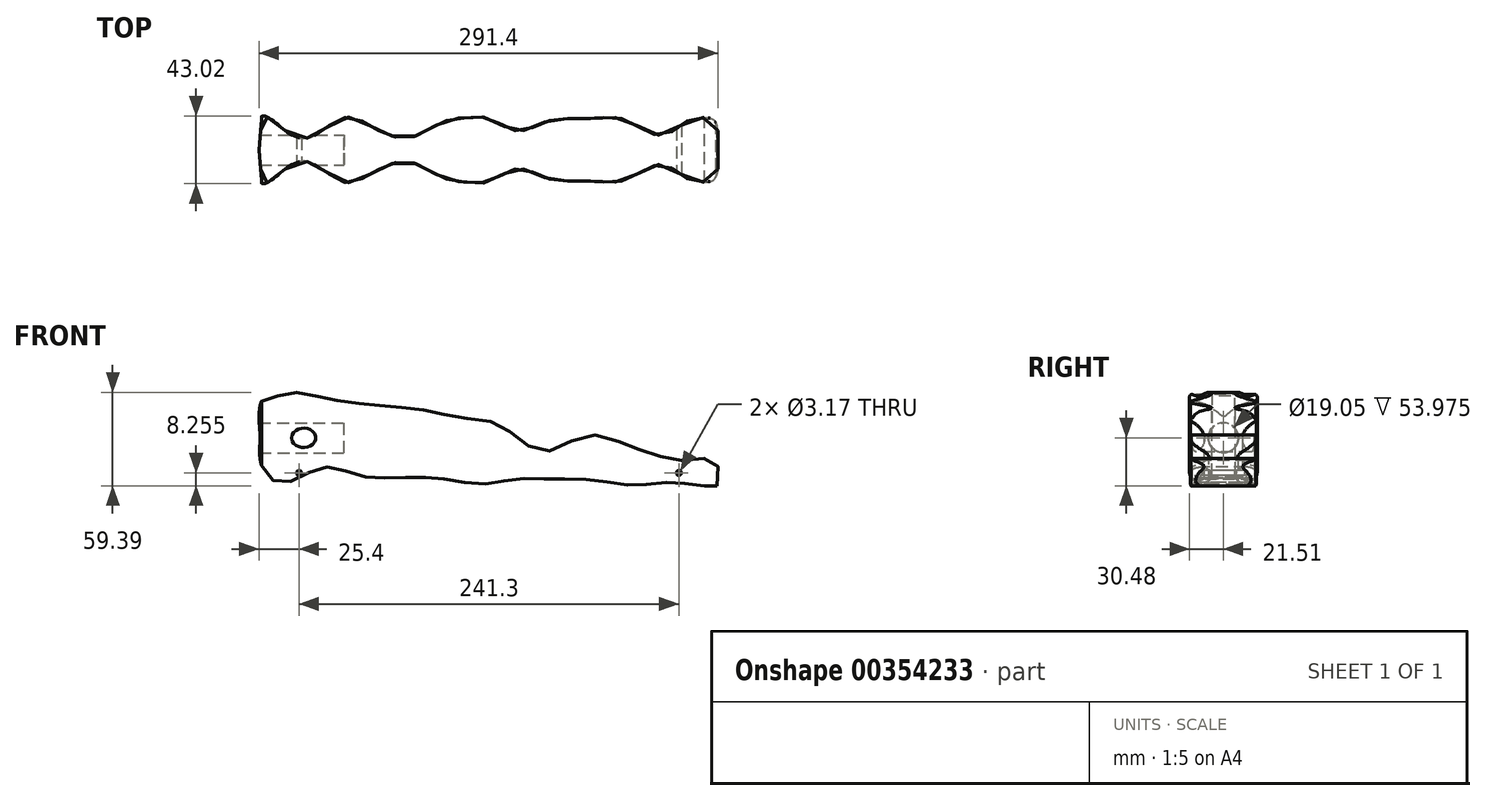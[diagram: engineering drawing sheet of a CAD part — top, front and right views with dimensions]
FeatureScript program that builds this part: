
annotation { "Feature Type Name" : "Feature", "Feature Type Description" : "" }
export const myFeature = defineFeature(function(context is Context, id is Id, definition is map)
    precondition{}
    {
        {
            var Q0;
            Q0=qCreatedBy(makeId("Front.planeOp"),FACE);
            var sketch = newSketch(context, id + "F0", { "sketchPlane" : qUnion([Q0])});
            skLineSegment(sketch, "E0.bottom", {"start": v(-146.05, 31.75) * mm, "end": v(146.05, 31.75) * mm, "construction": true});
            skLineSegment(sketch, "E0.top", {"start": v(-146.05, -31.75) * mm, "end": v(146.05, -31.75) * mm, "construction": true});
            skLineSegment(sketch, "E0.right", {"start": v(146.05, 31.75) * mm, "end": v(146.05, -31.75) * mm, "construction": true});
            skFitSpline(sketch, "E1", {"points": [v(-146.05, 0) * mm, v(-143.98, 24.56) * mm, v(-139.17, 27.47) * mm, v(-134.23, 26.49) * mm, v(-126.32, 28.75) * mm, v(-104.94, 25.5) * mm, v(-77, 21.23) * mm, v(-30.59, 15.63) * mm, v(-23.24, 12.77) * mm, v(4.3, 9.11) * mm, v(33.9, -8.77) * mm, v(59.13, 0.88) * mm, v(85.75, -3.53) * mm, v(117.37, -13.95) * mm, v(131.38, -13.42) * mm, v(144.88, -16) * mm, v(143.87, -27.24) * mm, v(144.82, -30.78) * mm, v(142.81, -31.18) * mm, v(115.14, -28.28) * mm, v(92.03, -30.12) * mm, v(63.45, -26.55) * mm, v(37.28, -26.3) * mm, v(14.94, -26.3) * mm, v(-3.83, -29.5) * mm, v(-26.85, -26.32) * mm, v(-55.1, -25.11) * mm, v(-81.78, -24.04) * mm, v(-105.32, -18.74) * mm, v(-127.18, -27.98) * mm, v(-141.83, -23.4) * mm, v(-146.05, 0) * mm]});
            skLineSegment(sketch, "E2.bottom", {"start": v(-146.05, 9.52) * mm, "end": v(-95.25, 9.52) * mm, "construction": true});
            skLineSegment(sketch, "E2.top", {"start": v(-141.83, -9.52) * mm, "end": v(-95.25, -9.52) * mm, "construction": true});
            skLineSegment(sketch, "E2.right", {"start": v(-95.25, 9.52) * mm, "end": v(-95.25, -9.52) * mm, "construction": true});
            skLineSegment(sketch, "E3", {"start": v(-146.05, 31.75) * mm, "end": v(-146.05, -31.75) * mm, "construction": true});
            skSolve(sketch);
        }
        {
            var Q0;
            Q0=qCreatedBy(makeId("Top.planeOp"),FACE);
            var sketch = newSketch(context, id + "F1", { "sketchPlane" : qUnion([Q0])});
            skLineSegment(sketch, "E4.bottom", {"start": v(-146.05, 22.22) * mm, "end": v(146.05, 22.23) * mm, "construction": true});
            skLineSegment(sketch, "E4.top", {"start": v(-146.05, -22.23) * mm, "end": v(146.05, -22.22) * mm, "construction": true});
            skLineSegment(sketch, "E4.left", {"start": v(-146.05, 22.22) * mm, "end": v(-146.05, -22.23) * mm, "construction": true});
            skLineSegment(sketch, "E4.right", {"start": v(146.05, 22.22) * mm, "end": v(146.05, -22.22) * mm, "construction": true});
            skLineSegment(sketch, "E5", {"start": v(-146.05, 0) * mm, "end": v(146.05, 0) * mm, "construction": true});
            skFitSpline(sketch, "E6", {"points": [v(-146.05, 0) * mm, v(-144.5, 19.86) * mm, v(-144.5, 21.15) * mm, v(-140.81, 20.87) * mm, v(-118.05, 7.23) * mm, v(-92.91, 20.25) * mm, v(-73.9, 14.46) * mm, v(-50.6, 7.57) * mm, v(-27.08, 18.63) * mm, v(-7.6, 20.48) * mm, v(0, 20.48) * mm, v(17.51, 12.02) * mm, v(37.61, 18.3) * mm, v(63.92, 19.8) * mm, v(86.18, 19.23) * mm, v(109.26, 9.28) * mm, v(127.86, 19.2) * mm, v(138.57, 20.35) * mm, v(143.71, 17.93) * mm, v(146.05, 0) * mm], "startDerivative": vector(0, 335.54) * mm, "endDerivative": vector(0, -277.49) * mm});
            skFitSpline(sketch, "E7.MirrorCS", {"points": [v(-146.05, 0) * mm, v(-144.5, -19.86) * mm, v(-144.5, -21.15) * mm, v(-140.81, -20.87) * mm, v(-118.05, -7.23) * mm, v(-92.91, -20.25) * mm, v(-73.9, -14.46) * mm, v(-50.6, -7.57) * mm, v(-27.08, -18.63) * mm, v(-7.6, -20.48) * mm, v(0, -20.48) * mm, v(17.51, -12.02) * mm, v(37.61, -18.3) * mm, v(63.92, -19.8) * mm, v(86.18, -19.23) * mm, v(109.26, -9.28) * mm, v(127.86, -19.2) * mm, v(138.57, -20.35) * mm, v(143.71, -17.93) * mm, v(146.05, 0) * mm], "startDerivative": vector(0, -335.54) * mm, "endDerivative": vector(0, 277.49) * mm});
            skLineSegment(sketch, "E8.MirrorCS", {"start": v(-146.05, -22.23) * mm, "end": v(146.05, -22.23) * mm});
            skSolve(sketch);
        }
        {
            var Q0;
            Q0=qCreatedBy(makeId("Right.planeOp"),FACE);
            var sketch = newSketch(context, id + "F2", { "sketchPlane" : qUnion([Q0])});
            skCircle(sketch, "E9", {"center": v(0, 0) * mm, "radius": 9.53 * mm});
            skSolve(sketch);
        }
        {
            var Q0;
            Q0=qCreatedBy(makeId("Front.planeOp"),FACE);
            var sketch = newSketch(context, id + "F3", { "sketchPlane" : qUnion([Q0])});
            skCircle(sketch, "E10", {"center": v(-120.65, -22.22) * mm, "radius": 1.59 * mm});
            skCircle(sketch, "E11", {"center": v(120.65, -22.23) * mm, "radius": 1.59 * mm});
            skSolve(sketch);
        }
        {
            var Q0;
            Q0=qSketchRegion(id+"F0",true);
            extrude(context, id + "F4", {"entities" : qUnion([Q0]), "depth" : 44.45 * mm, "symmetric" : true});
        }
        {
            var Q0;
            Q0=qSketchRegion(id+"F1",true);
            extrude(context, id + "F5", {"entities" : qUnion([Q0]), "operationType" : NewBodyOperationType.INTERSECT, "oppositeDirection" : true, "depth" : 60.96 * mm, "symmetric" : true});
        }
        {
            var Q0;
            Q0=qSketchRegion(id+"F2",true);
            extrude(context, id + "F6", {"entities" : qUnion([Q0]), "operationType" : NewBodyOperationType.REMOVE, "oppositeDirection" : true, "depth" : 152.4 * mm, "hasSecondDirection" : true, "secondDirectionOppositeDirection" : true, "secondDirectionDepth" : 92.07 * mm});
        }
        {
            var Q0;
            Q0=qSketchRegion(id+"F3",true);
            extrude(context, id + "F7", {"entities" : qUnion([Q0]), "operationType" : NewBodyOperationType.REMOVE, "oppositeDirection" : true, "depth" : 50.8 * mm, "symmetric" : true});
        }
    });
